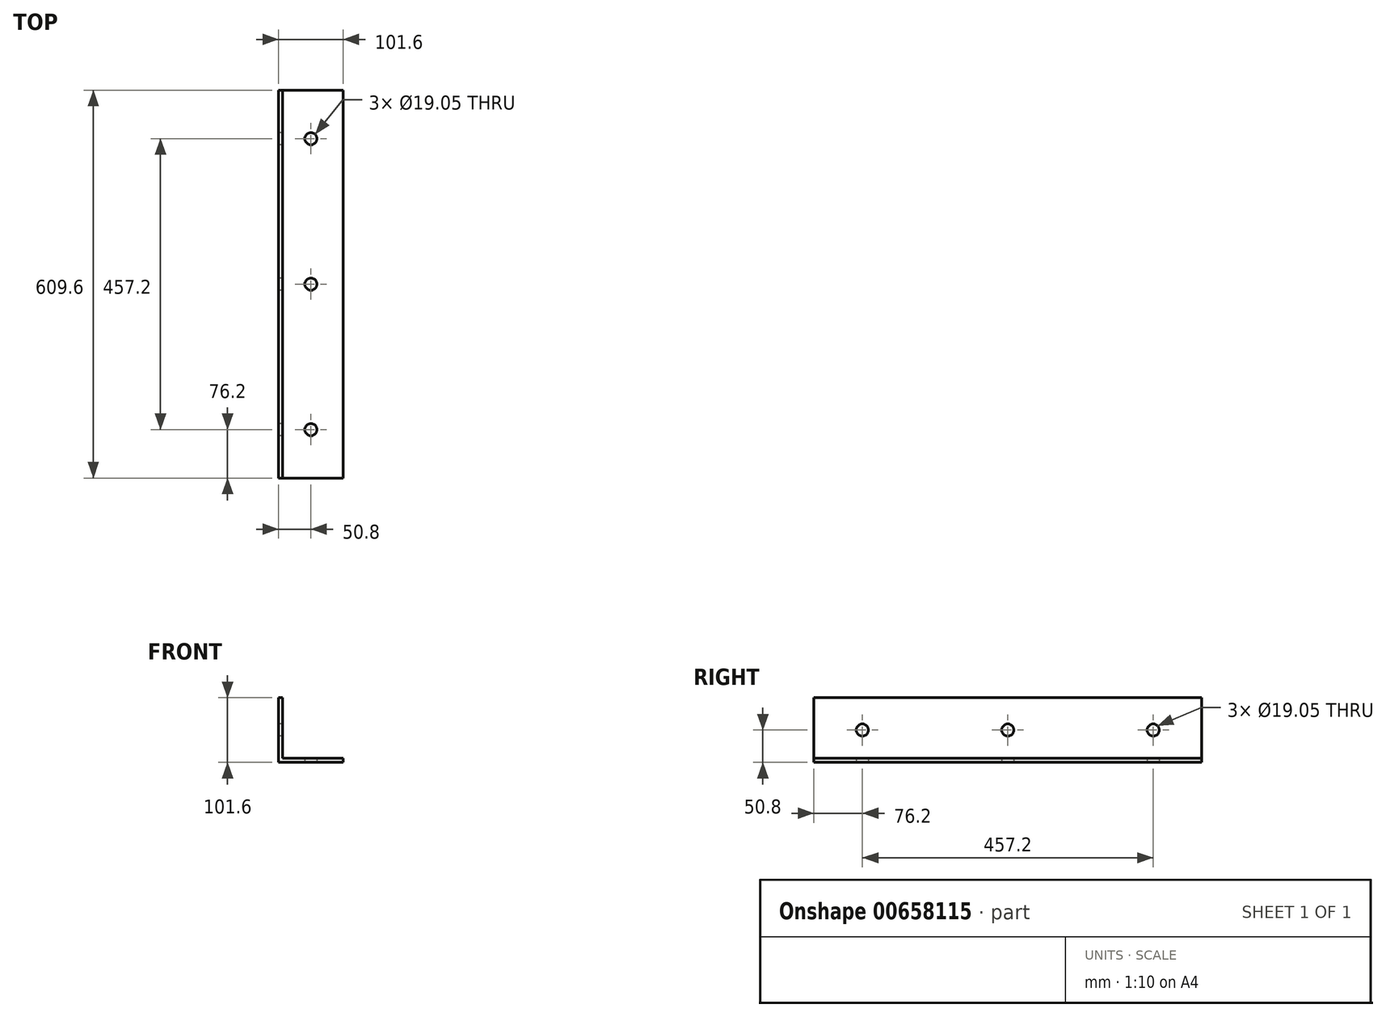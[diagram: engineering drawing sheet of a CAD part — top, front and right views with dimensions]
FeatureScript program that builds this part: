
annotation { "Feature Type Name" : "Feature", "Feature Type Description" : "" }
export const myFeature = defineFeature(function(context is Context, id is Id, definition is map)
    precondition{}
    {
        {
            var Q0;
            Q0=qCreatedBy(makeId("Front.planeOp"),FACE);
            var sketch = newSketch(context, id + "F0", { "sketchPlane" : qUnion([Q0])});
            skLineSegment(sketch, "E0", {"start": v(0, 0) * mm, "end": v(0, 101.6) * mm});
            skLineSegment(sketch, "E1", {"start": v(0, 101.6) * mm, "end": v(6.35, 101.6) * mm});
            skLineSegment(sketch, "E2", {"start": v(6.35, 101.6) * mm, "end": v(6.35, 6.35) * mm});
            skLineSegment(sketch, "E3", {"start": v(6.35, 6.35) * mm, "end": v(101.6, 6.35) * mm});
            skLineSegment(sketch, "E4", {"start": v(101.6, 6.35) * mm, "end": v(101.6, 0) * mm});
            skLineSegment(sketch, "E5", {"start": v(101.6, 0) * mm, "end": v(0, 0) * mm});
            skSolve(sketch);
        }
        {
            var Q0;
            Q0=makeQuery(id+"F0.imprint","IMPRINT",FACE,{"disambiguationData":[TD([[makeQuery(id+"F0.imprint","IMPRINT",EDGE,{"derivedFrom":sQuery(id+"F0.wireOp",EDGE,"E0")}),-1.0]])]});
            extrude(context, id + "F1", {"entities" : qUnion([Q0]), "oppositeDirection" : true, "depth" : 609.6 * mm, "offsetDistance" : 25.4 * mm});
        }
        {
            var Q0;
            Q0=makeQuery(id+"F1.opExtrude","SWEPT_FACE",FACE,{"disambiguationData":[OSD([sQuery(id+"F0.wireOp",EDGE,"E0")])]});
            var sketch = newSketch(context, id + "F2", { "sketchPlane" : qUnion([Q0])});
            skLineSegment(sketch, "E6", {"start": v(-620.26, 50.8) * mm, "end": v(63.4, 50.8) * mm, "construction": true});
            skLineSegment(sketch, "E7.0", {"start": v(-609.6, 101.6) * mm, "end": v(0, 101.6) * mm, "construction": true});
            skLineSegment(sketch, "E8.0", {"start": v(-609.6, 0) * mm, "end": v(-609.6, 101.6) * mm, "construction": true});
            skCircle(sketch, "E9", {"center": v(-533.4, 50.8) * mm, "radius": 9.53 * mm});
            skCircle(sketch, "E10", {"center": v(-304.8, 50.8) * mm, "radius": 9.53 * mm});
            skCircle(sketch, "E11", {"center": v(-76.2, 50.8) * mm, "radius": 9.53 * mm});
            skSolve(sketch);
        }
        {
            var Q0;
            Q0=qSketchRegion(id+"F2",true);
            extrude(context, id + "F3", {"entities" : qUnion([Q0]), "operationType" : NewBodyOperationType.REMOVE, "oppositeDirection" : true, "depth" : 25.4 * mm, "offsetDistance" : 25.4 * mm});
        }
        {
            var Q0;
            Q0=makeQuery(id+"F1.opExtrude","SWEPT_FACE",FACE,{"disambiguationData":[OSD([sQuery(id+"F0.wireOp",EDGE,"E5")])]});
            var sketch = newSketch(context, id + "F4", { "sketchPlane" : qUnion([Q0])});
            skLineSegment(sketch, "E12.0", {"start": v(101.6, -609.6) * mm, "end": v(101.6, 0) * mm, "construction": true});
            skLineSegment(sketch, "E12.1", {"start": v(101.6, -609.6) * mm, "end": v(0, -609.6) * mm, "construction": true});
            skLineSegment(sketch, "E13", {"start": v(50.8, 37.17) * mm, "end": v(50.8, -640.06) * mm, "construction": true});
            skCircle(sketch, "E14", {"center": v(50.8, -533.4) * mm, "radius": 9.53 * mm});
            skCircle(sketch, "E15", {"center": v(50.8, -304.8) * mm, "radius": 9.53 * mm});
            skCircle(sketch, "E16", {"center": v(50.8, -76.2) * mm, "radius": 9.53 * mm});
            skSolve(sketch);
        }
        {
            var Q0;
            Q0=qSketchRegion(id+"F4",true);
            extrude(context, id + "F5", {"entities" : qUnion([Q0]), "operationType" : NewBodyOperationType.REMOVE, "oppositeDirection" : true, "depth" : 25.4 * mm, "offsetDistance" : 25.4 * mm});
        }
    });
